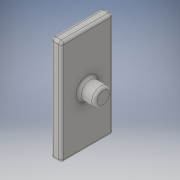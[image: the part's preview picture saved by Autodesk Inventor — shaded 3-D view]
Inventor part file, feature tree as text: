
AUTODESK INVENTOR PART (.ipt)
format: ipt  version: 2016 (Build 200138000, 138)  size: 138,240 bytes
history: native  units: mm
features: extrude x2, fillet x2, sketch x2
ambient origin geometry x8: Origin, YZ Plane, XZ Plane, XY Plane, X Axis, Y Axis, Z Axis, Center Point
bodies: Solid1 (feature_tree)
feature tree (6):
  extrude  "Extrusion1"  Depth=19.9mm
  extrude  "Extrusion2"  Depth=0.5mm
  fillet  "Fillet1"  Radius=3.0mm
  fillet  "Fillet2"  Radius=0.5mm
  sketch  "Sketch1"  dims[d0=9.9mm d1=19.9mm]
  sketch  "Sketch2"  dims[d2=2.0mm d3=0.0mm d4=3.3mm d5=3.0mm d6=0.0mm d7=0.5mm d8=0.5mm]
